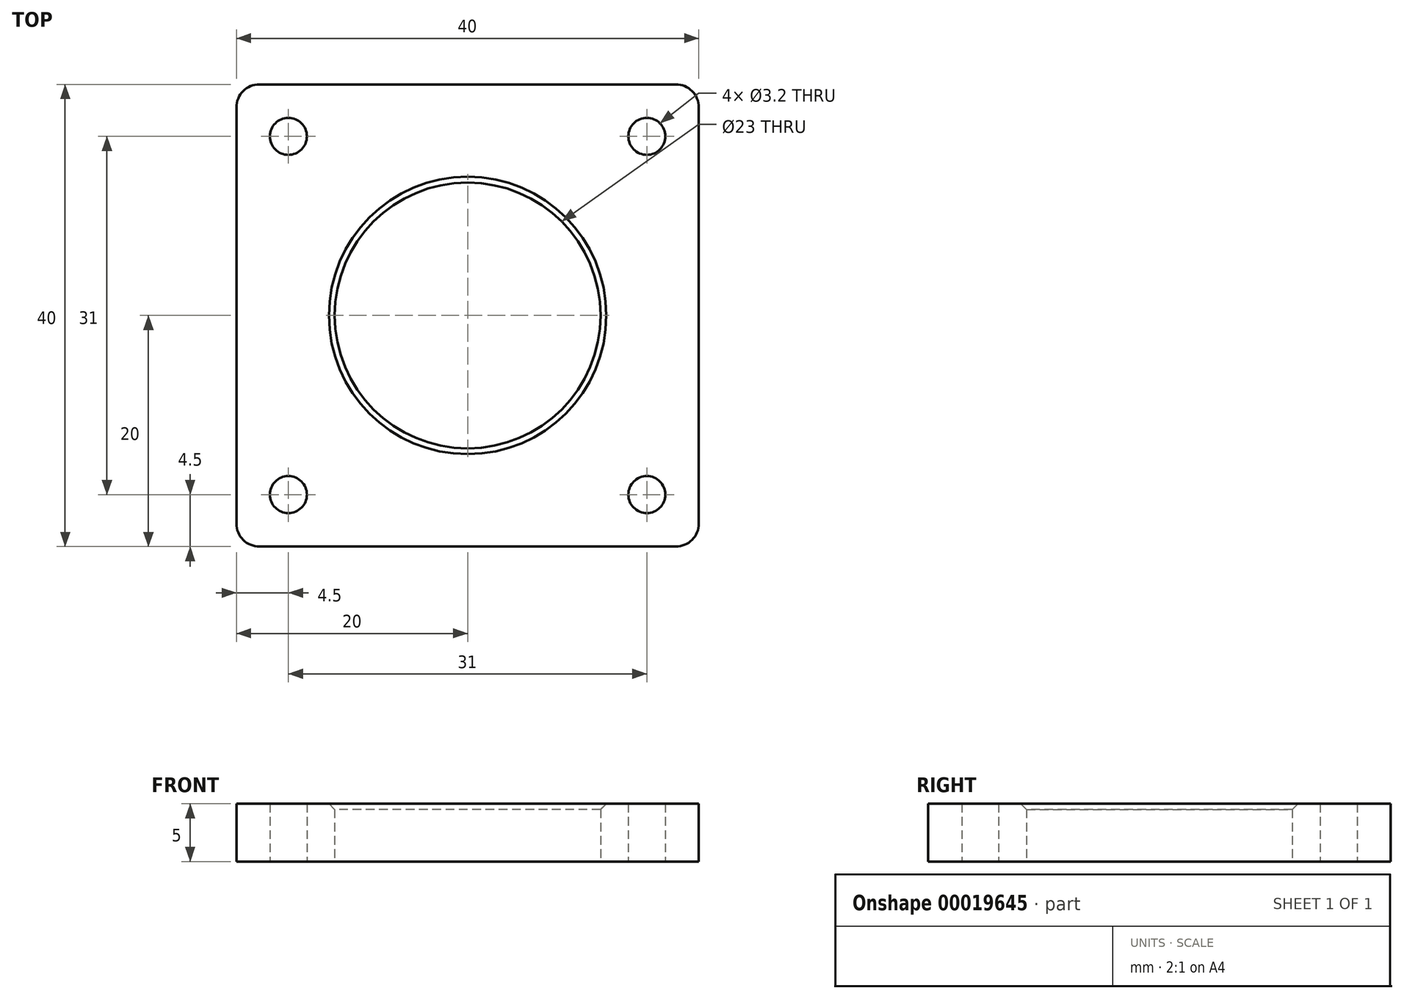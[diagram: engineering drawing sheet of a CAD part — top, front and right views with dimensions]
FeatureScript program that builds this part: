
annotation { "Feature Type Name" : "Feature", "Feature Type Description" : "" }
export const myFeature = defineFeature(function(context is Context, id is Id, definition is map)
    precondition{}
    {
        {
            var Q0;
            Q0=qCreatedBy(makeId("Top.planeOp"),FACE);
            var sketch = newSketch(context, id + "F0", { "sketchPlane" : qUnion([Q0])});
            skLineSegment(sketch, "E0.rect.bottom", {"start": v(20, 20) * mm, "end": v(-20, 20) * mm});
            skLineSegment(sketch, "E0.rect.top", {"start": v(20, -20) * mm, "end": v(-20, -20) * mm});
            skLineSegment(sketch, "E0.rect.left", {"start": v(20, 20) * mm, "end": v(20, -20) * mm});
            skLineSegment(sketch, "E0.rect.right", {"start": v(-20, 20) * mm, "end": v(-20, -20) * mm});
            skPoint(sketch, "E0.rect.middle", {"position": v(0, 0) * mm});
            skCircle(sketch, "E1", {"center": v(0, 0) * mm, "radius": 11.5 * mm});
            skCircle(sketch, "E2", {"center": v(-15.5, 15.5) * mm, "radius": 1.6 * mm});
            skCircle(sketch, "E3", {"center": v(15.5, 15.5) * mm, "radius": 1.6 * mm});
            skCircle(sketch, "E4", {"center": v(15.5, -15.5) * mm, "radius": 1.6 * mm});
            skCircle(sketch, "E5", {"center": v(-15.5, -15.5) * mm, "radius": 1.6 * mm});
            skSolve(sketch);
        }
        {
            var Q0;
            Q0 = qSketchRegion(id + "F0", true);
            extrude(context, id + "F1", {"entities" : qUnion([Q0]), "depth" : 5 * mm});
        }
        {
            var Q0;
            Q0=makeQuery(id+"F1.opExtrude","CAP_EDGE",EDGE,{"disambiguationData":[OSD([sQuery(id+"F0.wireOp",EDGE,"E1")])],"isStart":false});
            chamfer(context, id + "F2", {"entities" : qUnion([Q0]), "width" : 0.5 * mm, "tangentPropagation" : true});
        }
        {
            var Q0;
            Q0=makeQuery(id+"F1.opExtrude","SWEPT_EDGE",EDGE,{"disambiguationData":[OSD([sQuery(id+"F0.wireOp",EDGE,"E0.rect.top"),sQuery(id+"F0.wireOp",EDGE,"E0.rect.left")])]});
            var Q1;
            Q1=makeQuery(id+"F1.opExtrude","SWEPT_EDGE",EDGE,{"disambiguationData":[OSD([sQuery(id+"F0.wireOp",EDGE,"E0.rect.bottom"),sQuery(id+"F0.wireOp",EDGE,"E0.rect.left")])]});
            var Q2;
            Q2=makeQuery(id+"F1.opExtrude","SWEPT_EDGE",EDGE,{"disambiguationData":[OSD([sQuery(id+"F0.wireOp",EDGE,"E0.rect.top"),sQuery(id+"F0.wireOp",EDGE,"E0.rect.right")])]});
            var Q3;
            Q3=makeQuery(id+"F1.opExtrude","SWEPT_EDGE",EDGE,{"disambiguationData":[OSD([sQuery(id+"F0.wireOp",EDGE,"E0.rect.bottom"),sQuery(id+"F0.wireOp",EDGE,"E0.rect.right")])]});
            fillet(context, id + "F3", {"entities" : qUnion([Q0, Q1, Q2, Q3]), "radius" : 2 * mm, "tangentPropagation" : true, "allowEdgeOverflow" : false});
        }
    });
